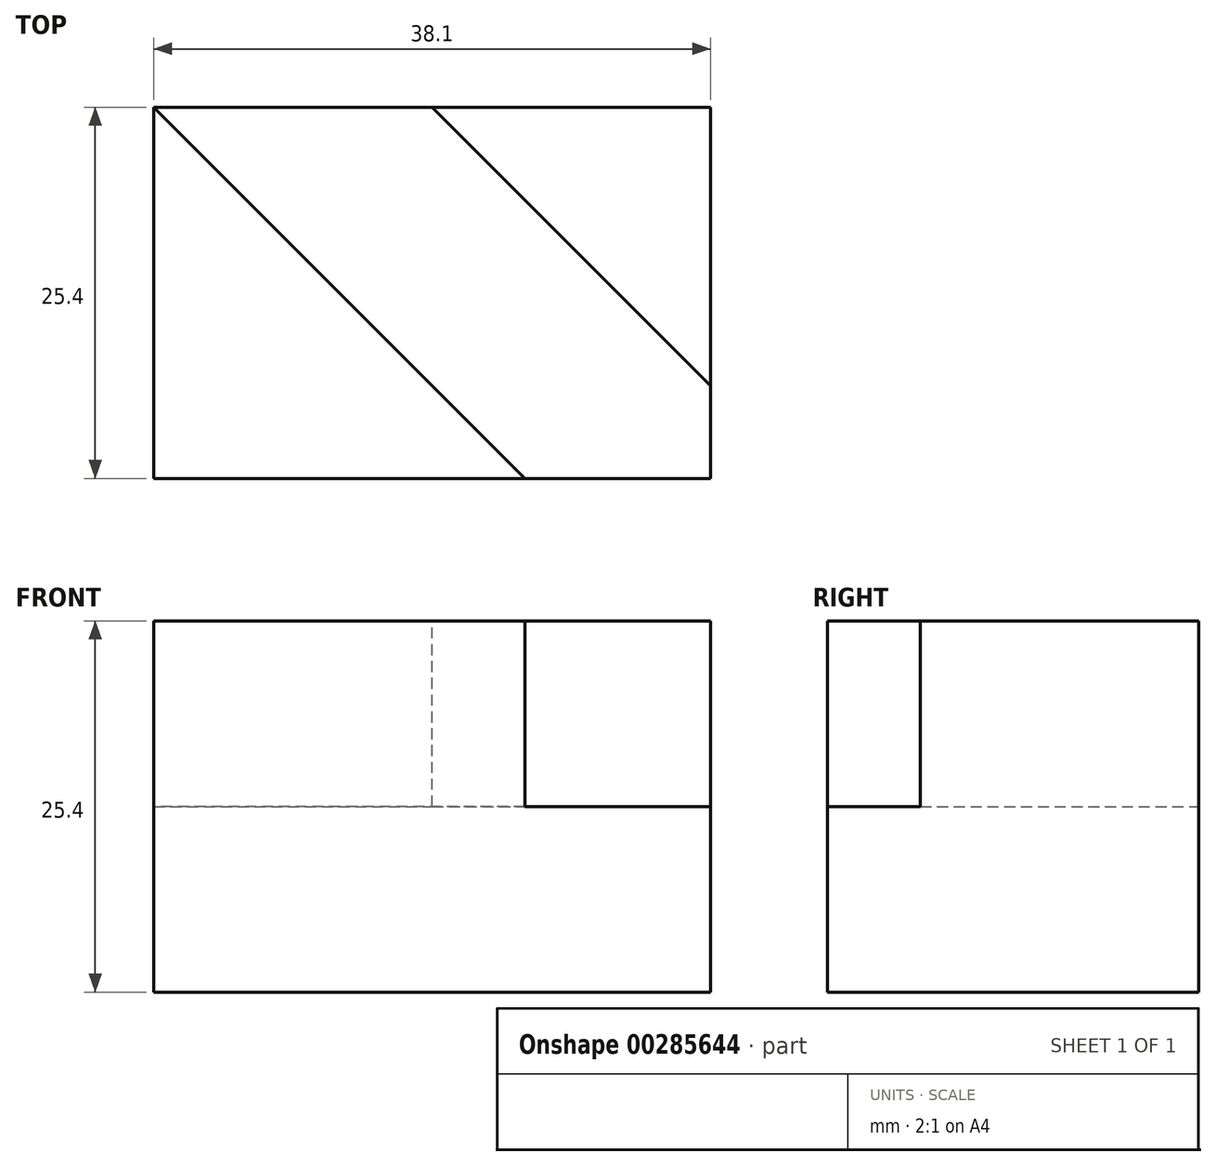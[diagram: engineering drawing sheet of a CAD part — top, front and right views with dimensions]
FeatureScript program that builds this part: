
annotation { "Feature Type Name" : "Feature", "Feature Type Description" : "" }
export const myFeature = defineFeature(function(context is Context, id is Id, definition is map)
    precondition{}
    {
        {
            var Q0;
            Q0=qCreatedBy(makeId("Front.planeOp"),FACE);
            var sketch = newSketch(context, id + "F0", { "sketchPlane" : qUnion([Q0])});
            skLineSegment(sketch, "E0.bottom", {"start": v(0, 0) * mm, "end": v(38.1, 0) * mm});
            skLineSegment(sketch, "E0.top", {"start": v(0, 25.4) * mm, "end": v(38.1, 25.4) * mm});
            skLineSegment(sketch, "E0.left", {"start": v(0, 0) * mm, "end": v(0, 25.4) * mm});
            skLineSegment(sketch, "E0.right", {"start": v(38.1, 0) * mm, "end": v(38.1, 25.4) * mm});
            skSolve(sketch);
        }
        {
            var Q0;
            Q0 = qSketchRegion(id + "F0", true);
            extrude(context, id + "F1", {"entities" : qUnion([Q0]), "oppositeDirection" : true, "depth" : 25.4 * mm});
        }
        {
            var Q0;
            Q0=makeQuery(id+"F1.opExtrude","CAP_FACE",FACE,{"disambiguationData":[OSD([sQuery(id+"F0.wireOp",EDGE,"E0.bottom"),sQuery(id+"F0.wireOp",EDGE,"E0.top"),sQuery(id+"F0.wireOp",EDGE,"E0.left"),sQuery(id+"F0.wireOp",EDGE,"E0.right")])],"isStart":true});
            var sketch = newSketch(context, id + "F2", { "sketchPlane" : qUnion([Q0])});
            skLineSegment(sketch, "E1", {"start": v(25.4, 25.4) * mm, "end": v(25.4, 12.7) * mm});
            skLineSegment(sketch, "E2", {"start": v(25.4, 12.7) * mm, "end": v(38.1, 12.7) * mm});
            skLineSegment(sketch, "E3", {"start": v(25.4, 25.4) * mm, "end": v(38.1, 25.4) * mm});
            skLineSegment(sketch, "E4", {"start": v(38.1, 25.4) * mm, "end": v(38.1, 12.7) * mm});
            skSolve(sketch);
        }
        {
            var Q0;
            Q0 = qSketchRegion(id + "F2", true);
            extrude(context, id + "F3", {"entities" : qUnion([Q0]), "operationType" : NewBodyOperationType.REMOVE, "oppositeDirection" : true, "depth" : 6.35 * mm});
        }
        {
            var Q0;
            Q0=makeQuery(id+"F1.opExtrude","SWEPT_FACE",FACE,{"disambiguationData":[OSD([sQuery(id+"F0.wireOp",EDGE,"E0.top")])]});
            var sketch = newSketch(context, id + "F4", { "sketchPlane" : qUnion([Q0])});
            skLineSegment(sketch, "E5", {"start": v(25.4, 0) * mm, "end": v(0, 25.4) * mm});
            skLineSegment(sketch, "E6", {"start": v(0, 25.4) * mm, "end": v(19.05, 25.4) * mm});
            skLineSegment(sketch, "E7", {"start": v(19.05, 25.4) * mm, "end": v(38.1, 6.35) * mm});
            skLineSegment(sketch, "E8", {"start": v(38.1, 6.35) * mm, "end": v(25.4, 6.35) * mm});
            skLineSegment(sketch, "E9", {"start": v(25.4, 6.35) * mm, "end": v(25.4, 1.12) * mm});
            skSolve(sketch);
        }
        {
            var Q0;
            Q0 = qSketchRegion(id + "F4", true);
            var Q1;
            {var subQ0=sQuery(id+"F4.wireOp",EDGE,"E5");Q1=makeQuery(id+"F4.imprint","IMPRINT",FACE,{"disambiguationData":[TD([[makeQuery(id+"F4.imprint","IMPRINT",EDGE,{"derivedFrom":subQ0}),-1.0]])]});}
            extrude(context, id + "F5", {"entities" : qUnion([Q0, Q1]), "operationType" : NewBodyOperationType.REMOVE, "oppositeDirection" : true, "depth" : 12.7 * mm});
        }
    });
